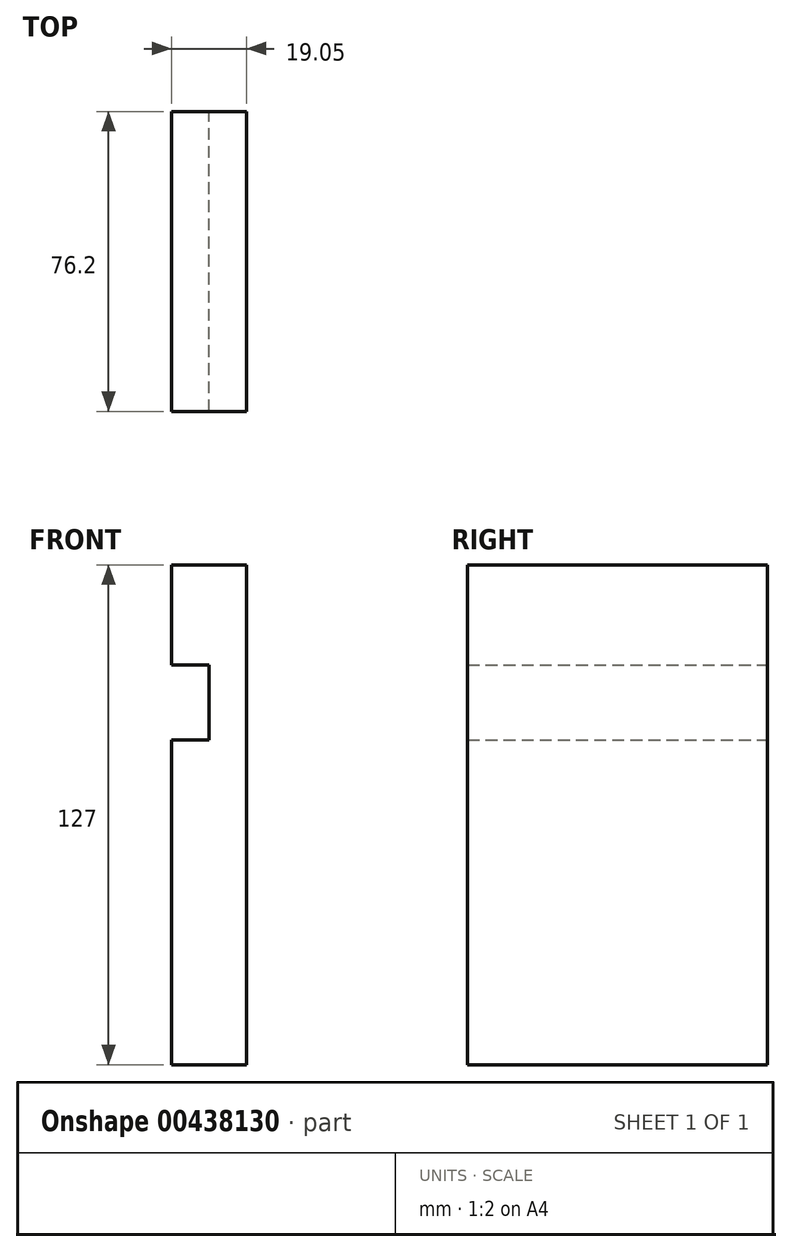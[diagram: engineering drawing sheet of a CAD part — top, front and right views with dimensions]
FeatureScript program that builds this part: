
annotation { "Feature Type Name" : "Feature", "Feature Type Description" : "" }
export const myFeature = defineFeature(function(context is Context, id is Id, definition is map)
    precondition{}
    {
        {
            var Q0;
            Q0=qCreatedBy(makeId("Front.planeOp"),FACE);
            var sketch = newSketch(context, id + "F0", { "sketchPlane" : qUnion([Q0])});
            skLineSegment(sketch, "E0", {"start": v(24.82, -71.6) * mm, "end": v(43.87, -71.6) * mm});
            skLineSegment(sketch, "E1", {"start": v(43.87, -71.6) * mm, "end": v(43.87, 55.4) * mm});
            skLineSegment(sketch, "E2", {"start": v(43.87, 55.4) * mm, "end": v(24.82, 55.4) * mm});
            skLineSegment(sketch, "E3", {"start": v(24.82, 55.4) * mm, "end": v(24.82, 30) * mm});
            skLineSegment(sketch, "E4", {"start": v(24.82, 30) * mm, "end": v(34.35, 30) * mm});
            skLineSegment(sketch, "E5", {"start": v(34.35, 30) * mm, "end": v(34.35, 10.94) * mm});
            skLineSegment(sketch, "E6", {"start": v(34.35, 10.94) * mm, "end": v(24.82, 10.94) * mm});
            skLineSegment(sketch, "E7", {"start": v(24.82, 10.94) * mm, "end": v(24.82, -71.6) * mm});
            skSolve(sketch);
        }
        {
            var Q0;
            Q0 = qSketchRegion(id + "F0", true);
            extrude(context, id + "F1", {"entities" : qUnion([Q0]), "depth" : 76.2 * mm});
        }
    });
